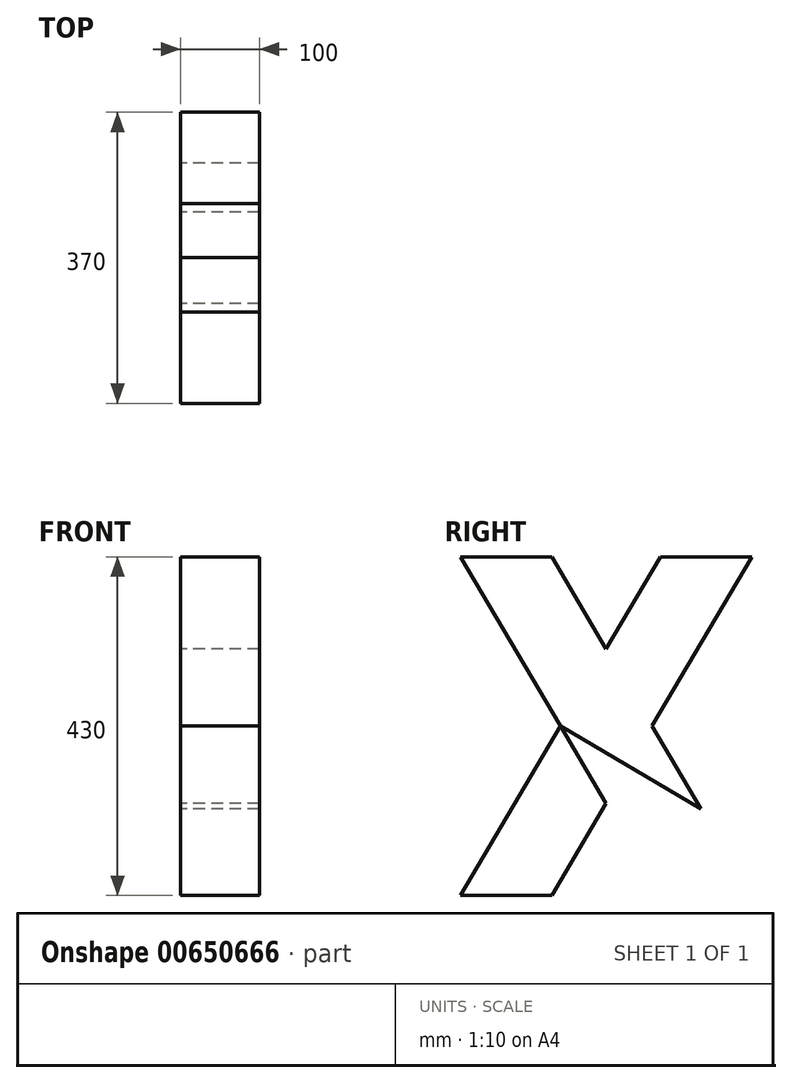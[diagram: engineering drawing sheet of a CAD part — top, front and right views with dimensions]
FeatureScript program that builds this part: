
annotation { "Feature Type Name" : "Feature", "Feature Type Description" : "" }
export const myFeature = defineFeature(function(context is Context, id is Id, definition is map)
    precondition{}
    {
        {
            var Q0;
            Q0=qCreatedBy(makeId("Right.planeOp"),FACE);
            var sketch = newSketch(context, id + "F0", { "sketchPlane" : qUnion([Q0])});
            skLineSegment(sketch, "E0", {"start": v(-185, -225) * mm, "end": v(-68.87, -225) * mm});
            skLineSegment(sketch, "E1", {"start": v(-185, 205) * mm, "end": v(-68.87, 205) * mm});
            skLineSegment(sketch, "E2", {"start": v(-185, 205) * mm, "end": v(68.87, -225) * mm});
            skLineSegment(sketch, "E3", {"start": v(-68.87, 205) * mm, "end": v(185, -225) * mm});
            skLineSegment(sketch, "E4", {"start": v(185, 205) * mm, "end": v(58.06, -10) * mm});
            skLineSegment(sketch, "E5", {"start": v(68.87, 205) * mm, "end": v(0, 88.35) * mm});
            skLineSegment(sketch, "E6.trimOffspring", {"start": v(68.87, 205) * mm, "end": v(185, 205) * mm});
            skLineSegment(sketch, "E7.trimOffspring", {"start": v(-58.06, -10) * mm, "end": v(-185, -225) * mm});
            skLineSegment(sketch, "E8.trimOffspring", {"start": v(0, -108.35) * mm, "end": v(-68.87, -225) * mm});
            skLineSegment(sketch, "E9.trimOffspring", {"start": v(68.87, -225) * mm, "end": v(185, -225) * mm});
            skLineSegment(sketch, "E10", {"start": v(-58.06, -10) * mm, "end": v(174.42, -147.26) * mm});
            skLineSegment(sketch, "E11", {"start": v(-185, 205) * mm, "end": v(0, 314.22) * mm});
            skLineSegment(sketch, "E12", {"start": v(185, -225) * mm, "end": v(-39.88, -357.77) * mm});
            skLineSegment(sketch, "E13", {"start": v(-185, -225) * mm, "end": v(-38.41, -311.55) * mm});
            skSolve(sketch);
        }
        {
            var Q0;
            Q0=makeQuery(id+"F0.imprint","IMPRINT",FACE,{"disambiguationData":[TD([[makeQuery(id+"F0.imprint","IMPRINT",EDGE,{"derivedFrom":sQuery(id+"F0.wireOp",EDGE,"E0")}),1.0]])]});
            var Q1;
            {var subQ0=sQuery(id+"F0.wireOp",EDGE,"E4");Q1=makeQuery(id+"F0.imprint","IMPRINT",FACE,{"disambiguationData":[TD([[makeQuery(id+"F0.imprint","IMPRINT",EDGE,{"derivedFrom":subQ0}),-1.0]])]});}
            var Q2;
            {var subQ4=sQuery(id+"F0.wireOp",EDGE,"E1");Q2=makeQuery(id+"F0.imprint","IMPRINT",FACE,{"disambiguationData":[TD([[makeQuery(id+"F0.imprint","IMPRINT",EDGE,{"derivedFrom":subQ4}),-1.0]])]});}
            extrude(context, id + "F1", {"entities" : qUnion([Q0, Q1, Q2]), "endBound" : BoundingType.SYMMETRIC, "depth" : 100 * mm, "offsetDistance" : 25 * mm});
        }
    });
